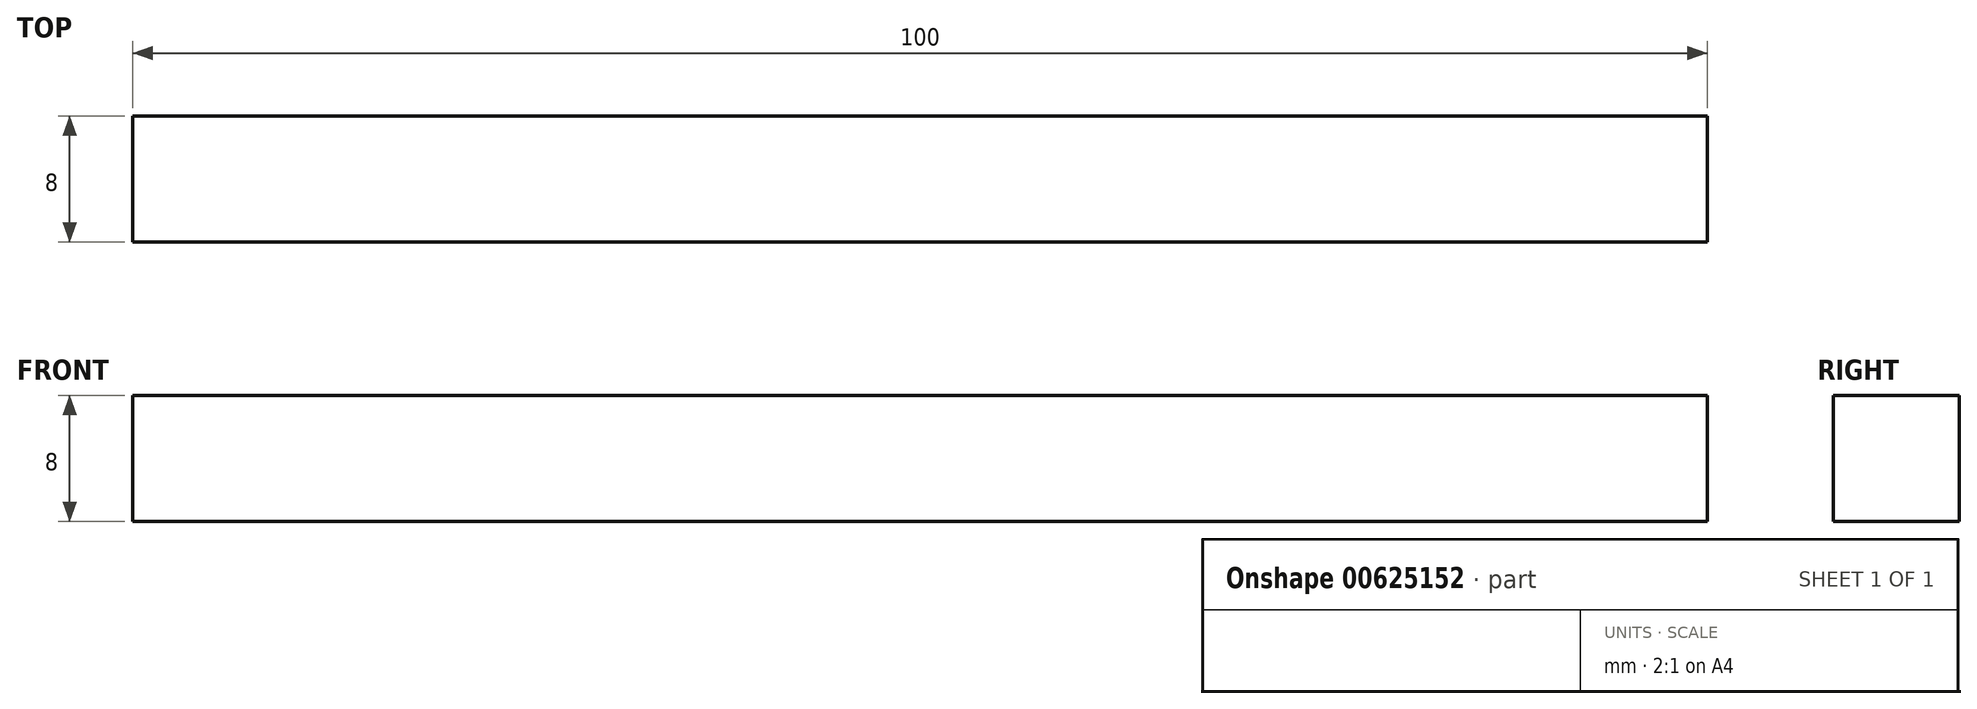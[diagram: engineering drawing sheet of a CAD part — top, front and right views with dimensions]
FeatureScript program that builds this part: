
annotation { "Feature Type Name" : "Feature", "Feature Type Description" : "" }
export const myFeature = defineFeature(function(context is Context, id is Id, definition is map)
    precondition{}
    {
        {
            var Q0;
            Q0=qCreatedBy(makeId("Top.planeOp"),FACE);
            var sketch = newSketch(context, id + "F0", { "sketchPlane" : qUnion([Q0])});
            skLineSegment(sketch, "E0.bottom", {"start": v(50, 4) * mm, "end": v(-50, 4) * mm});
            skLineSegment(sketch, "E0.top", {"start": v(50, -4) * mm, "end": v(-50, -4) * mm});
            skLineSegment(sketch, "E0.left", {"start": v(50, 4) * mm, "end": v(50, -4) * mm});
            skLineSegment(sketch, "E0.right", {"start": v(-50, 4) * mm, "end": v(-50, -4) * mm});
            skPoint(sketch, "E0.middle", {"position": v(0, 0) * mm});
            skSolve(sketch);
        }
        {
            var Q0;
            Q0=makeQuery(id+"F0.imprint","IMPRINT",FACE,{"disambiguationData":[TD([[makeQuery(id+"F0.imprint","IMPRINT",EDGE,{"derivedFrom":sQuery(id+"F0.wireOp",EDGE,"E0.bottom")}),1.0]])]});
            extrude(context, id + "F1", {"entities" : qUnion([Q0]), "depth" : 8 * mm, "offsetDistance" : 25 * mm});
        }
    });
